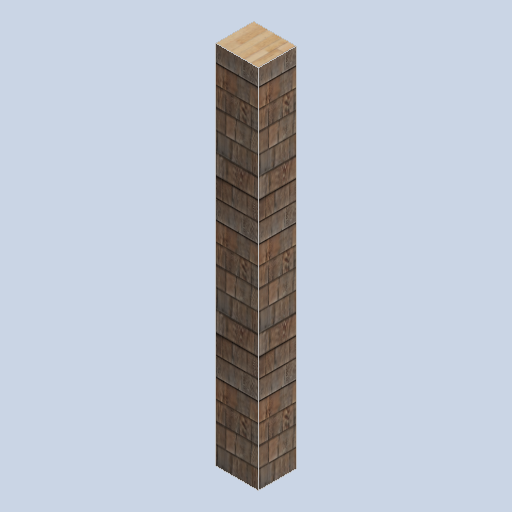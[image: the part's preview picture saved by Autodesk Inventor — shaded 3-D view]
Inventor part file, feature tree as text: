
AUTODESK INVENTOR PART (.ipt)
format: ipt  version: 2024.2 (Build 282272000, 272)  size: 349,184 bytes
history: native  units: mm
features: extrude x1, sketch x1
ambient origin geometry x8: Origin, YZ Plane, XZ Plane, XY Plane, X Axis, Y Axis, Z Axis, Center Point
bodies: Solid1 (feature_tree)
feature tree (2):
  extrude  "Extrusion1"  Depth=310.0mm
  sketch  "Sketch1"  dims[d0=350.0mm d1=310.0mm d2=3000.0mm d3=0.0mm]
